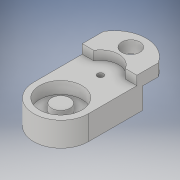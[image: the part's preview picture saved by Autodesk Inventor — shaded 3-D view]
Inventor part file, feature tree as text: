
AUTODESK INVENTOR PART (.ipt)
format: ipt  version: 2018 (Build 220112000, 112)  size: 164,864 bytes
history: native  units: in
note: dims shown in document units (in); Inventor stores cm internally (conversion verified against a paired STEP export)
features: extrude x8, sketch x8
ambient origin geometry x8: Origin, YZ Plane, XZ Plane, XY Plane, X Axis, Y Axis, Z Axis, Center Point
bodies: Solid1 (feature_tree)
feature tree (16):
  extrude  "Extrusion1"  Depth=0.0787in
  extrude  "Extrusion2"  Depth=0.2362in
  extrude  "Extrusion3"  Depth=0.1575in TaperAngle=0.0deg
  extrude  "Extrusion4"  Depth=0.7087in
  extrude  "Extrusion5"  Depth=0.1181in
  extrude  "Extrusion6"  Depth=0.2756in TaperAngle=0.0deg
  extrude  "Extrusion7"  Depth=0.1181in TaperAngle=0.0deg
  extrude  "Extrusion9"  [1 undecoded]
  sketch  "Sketch1"  dims[d6=0.0787in d8=0.0787in]
  sketch  "Sketch2"  dims[d9=0.315in d10=0.0in d11=0.2362in]
  sketch  "Sketch3"  dims[d12=0.5512in d13=0.1575in d14=0.0in]
  sketch  "Sketch4"  dims[d15=0.0591in d16=0.0in d17=0.7087in]
  sketch  "Sketch6"  dims[d21=0.1181in d22=0.0in d23=0.4724in]
  sketch  "Sketch7"  dims[d24=0.2756in d25=0.0in d26=0.2756in d27=0.0in]
  sketch  "Sketch8"  dims[d28=0.2756in d29=0.0in d35=0.1181in d36=0.0in]
  sketch  "Sketch11"  dims[d38=0.4724in]
note: 1 required parameter value undecoded (feature->parameter linkage not recoverable at this tier; creation-order binding heuristic only, values carry confidence <= 0.55)
